# Revit family: NBS_DudleyIndustriesLimited_WsteBins_Platinum30LWasteBin
name_source: partatom
category: Furniture
revit_build: Autodesk Revit 2018 (Build: 20190510_1515(x64)
units: mm (PartAtom-declared; Revit-internal decimal feet)

## family parameters
Always vertical = Yes
Cut with Voids When Loaded = No
Room Calculation Point = No
Shared = No
Work Plane-Based = No

## types (1)
- Platinum30LWasteBin
    AssetType = Fixed
    BIMObjectName = NBS_DudleyIndustriesLimited_WasteBins_Platinum30LWasteBin
    BinMaterial = NBS_DudleyIndustriesLimited_StainlessSteel_Brushed
    Category = Pr_40_50_07_96:Waste bins
    Color = Brushed with clear lacquer
    Description = 30L waste bin with open top
    DurationUnit = year
    Features = Can be free standing or wall mounted, innovative coating helps prevent fingerprint marks
    Finish = Brushed with clear lacquer
    FinishAndColour = Brushed with clear lacquer
    IfcExportAs = IfcFurnitureType
    IfcExportType = UNDEFINED
    IsBuiltIn = No
    ManufacturerName = Dudley Industries Limited
    ManufacturerURL = www.dudleyindustries.com
    Material = Stainless steel
    Materials = Stainless steel
    ModelNumber = 77020CB
    ModelReference = Platinum30LWasteBin
    NBSCertification = www.nationalbimlibrary.com/cert/3pw53nwn
    NBSDescription = Waste bins
    NBSReference = 45-35-72/380
    Name = WasteBins_Platinum30LWasteBin_DudleyIndustriesLimited
    NominalDepth = 236 mm
    NominalHeight = 603 mm
    NominalLength = 0 mm  [stored 0 ft]
    NominalWidth = 332 mm
    ProductInformation = https://www.dudleyindustries.com
    Shape = Rectangular
    Size = 236 x 603 x 332 mm
    Status = UNSET
    Style = Bin
    Uniclass2015Code = Pr_40_50_07_96
    Uniclass2015Title = Waste bins
    Uniclass2015Version = Products v1.18
    Version = 1
    WarrantyDescription = 10 Years
    WarrantyDurationUnit = year
    Weight = 5 kg

note: [stored X ft] marks values corroborated as IEEE doubles in the binary element streams (Revit-internal decimal feet)

## geometry (parser evidence)
native form markers: Sweep x3
no freeform markers — native parametric forms only
